# Revit family: Grinder_Pump-Hazardous_Environment-Zoeller-X7012_X7013_Series
name_source: partatom
category: Mechanical Equipment
revit_build: Autodesk Revit 2014 (Build: 20130308_1515(x64)
units: mm (PartAtom-declared; Revit-internal decimal feet)

## types (12) — shared parameters
Assembly Code = D2010900
Cutter & Plate = SS Hardened to 55-60 Rockwell
Default Elevation = 0"
Description = Commercial Effluent Pumps
Discharge Diameter = 1.25" NPT
Discharge Height = 5"
Discharge Radius = 5/8"
Hertz = 60
Impeller Type = Vortex (Bronze)
Installation Type = Floor Mounted
Insulation = Class F
Lead Wires Insulation = Class F
Length = 11 27/32"
Manufacturer = Zoeller
Material = Cast Iron-Zoeller-Powder Coated Epoxy
Max. Stator Temp. = 311 °F
Max. Water Temp. = 104 °F
Maximum KW Input = 3.9
Model = X7012
Moisture Sensor = Moisture Sensing Probes (Requires a circuit in control panel)
Motor = 2.0 Pump Name Plate Horsepower
Motor Shaft = 416 S.S.
Motor Thermal Shutoff = Thermal Sensors
Motor Type = Submersible Explosion Proof
NEC Locked Rotor Code = K
O-Rings = Viton
Operation = Non-Automatic
Overall Height = 26 1/2"
Power Cord = 14 Gauge SOW
Price = Prices may vary. Please consult Manufacturer Representative for most up-to-date price list.
Product Page URL = http://www.zoellerengprod.com
RPM = 3450
Service Factor = 1.2
Shaft Seal Lower (Options) = Silicon Carbide/Silicon Carbide
Shaft Seal Lower Standard = Carbon/Silicon Carbide
Shaft Seal Upper (Options) = Carbon/Silicon Carbide, Silicon Carbide/Silicon Carbide
Shaft Seal Upper Standard = Carbon/Ceramic
Tandem Seals = Standard
Type SOW Power Cord Length = 240"
URL = http://www.zoellerengprod.com
Warranty Information = 36 Months (Limited)
Waste Connection = Yes
Width = 8 1/2"

## per-type parameters (varying)
| type | Apparent Load | Configuration | Flow @ 5' | Full Load Amps (Voltage Dependent) | Impeller Diameter | Locked Rotor Amps | Motor Design Letter | Phase | Shipping Weight | Type | Voltage |
| X7012 - 200V 1Ph | 1220 VA | High Head | 34 GPM | 20.0 | 6 1/8" | 60.7 | NEMA L | 1 | 139 lbs. | Split Capacitor | 200 V |
| X7012 - 230V 1Ph | 1150 VA | High Head | 34 GPM | 17.2 | 6 1/8" | 57.3 | NEMA L | 1 | 139 lbs. | Split Capacitor | 230 V |
| X7012 - 200V 3Ph | 720 VA | High Head | 34 GPM | 12.3 | 6 1/8" | 47.0 | NEMA B | 3 | 132 lbs. | 3 Phase | 200 V |
| X7012 - 230V 3Ph | 690 VA | High Head | 34 GPM | 10.8 | 6 1/8" | 41.9 | NEMA B | 3 | 132 lbs. | 3 Phase | 230 V |
| X7012 - 460V 3Ph | 782 VA | High Head | 34 GPM | 5.5 | 6 1/8" | 20.6 | NEMA B | 3 | 132 lbs. | 3 Phase | 460 V |
| X7012 - 575V 3Ph | 805 VA | High Head | 34 GPM | 4.5 | 6 1/8" | 16.2 | NEMA B | 3 | 132 lbs. | 3 Phase | 575 V |
| X7013 - 575V 3Ph | 805 VA | High Flow | 59 GPM | 4.5 | 6 3/16" | 16.2 | NEMA B | 3 | 132 lbs. | 3 Phase | 575 V |
| X7013 - 200V 1Ph | 1220 VA | High Flow | 59 GPM | 20.0 | 6 3/16" | 60.7 | NEMA L | 1 | 139 lbs. | Split Capacitor | 200 V |
| X7013 - 200V 3Ph | 720 VA | High Flow | 59 GPM | 12.3 | 6 3/16" | 47.0 | NEMA B | 3 | 132 lbs. | 3 Phase | 200 V |
| X7013 - 230V 1Ph | 1150 VA | High Flow | 59 GPM | 17.2 | 6 3/16" | 57.3 | NEMA L | 1 | 139 lbs. | Split Capacitor | 230 V |
| X7013 - 230V 3Ph | 690 VA | High Flow | 59 GPM | 10.8 | 6 3/16" | 41.9 | NEMA B | 3 | 132 lbs. | 3 Phase | 230 V |
| X7013 - 460V 3Ph | 782 VA | High Flow | 59 GPM | 5.5 | 6 3/16" | 20.6 | NEMA B | 3 | 132 lbs. | 3 Phase | 460 V |

## geometry (parser evidence)
native form markers: Sweep x1
no freeform markers — native parametric forms only
